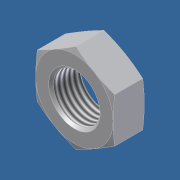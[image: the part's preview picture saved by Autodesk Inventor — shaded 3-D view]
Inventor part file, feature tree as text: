
AUTODESK INVENTOR PART (.ipt)
format: ipt  version: 2012 (Build 160160000, 160)  size: 129,024 bytes
history: native  units: in
note: dims shown in document units (in); Inventor stores cm internally (conversion verified against a paired STEP export)
features: other x70, sketch x3, revolve x2, extrude x1, thread x1
ambient origin geometry x8: Origin, YZ Plane, XZ Plane, XY Plane, X Axis, Y Axis, Z Axis, Center Point
bodies: Solid1 (feature_tree)
feature tree (77):
  sketch  "Sketch_8"  dims[d0=360.0deg d1=0.38in d2=0.0in]
  sketch  "Sketch_10"  dims[d3=360.0deg d4=0.38in d5=0.0in]
  revolve  "Revolution1"  [1 undecoded]
  extrude  "Extrusion1"  Depth=0.38in TaperAngle=0.0deg
  revolve  "Revolution2"  [1 undecoded]
  thread  "Thread1"  [1 undecoded]
  other  "NUT_XY"
  other  "NUT_YZ"
  other  "NUT_ZX"
  other  "NUT_X"
  other  "NUT_Y"
  other  "NUT_Z"
  other  "NUT_Center"
  other  "a1_XY"
  other  "a1_YZ"
  other  "a1_ZX"
  other  "a1_X"
  other  "a1_Y"
  other  "a1_Z"
  other  "a1_Center"
  other  "a2_XY"
  other  "a2_YZ"
  other  "a2_ZX"
  other  "a2_X"
  other  "a2_Y"
  other  "a2_Z"
  other  "a2_Center"
  other  "b1_XY"
  other  "b1_YZ"
  other  "b1_ZX"
  other  "b1_X"
  other  "b1_Y"
  other  "b1_Z"
  other  "b1_Center"
  other  "b2_XY"
  other  "b2_YZ"
  other  "b2_ZX"
  other  "b2_X"
  other  "b2_Y"
  other  "b2_Z"
  other  "b2_Center"
  other  "e_XY"
  other  "e_YZ"
  other  "e_ZX"
  other  "e_X"
  other  "e_Y"
  other  "e_Z"
  other  "e_Center"
  other  "th1_XY"
  other  "th1_YZ"
  other  "th1_ZX"
  other  "th1_X"
  other  "th1_Y"
  other  "th1_Z"
  other  "th1_Center"
  other  "th2_XY"
  other  "th2_YZ"
  other  "th2_ZX"
  other  "th2_X"
  other  "th2_Y"
  other  "th2_Z"
  other  "th2_Center"
  other  "ol1_XY"
  other  "ol1_YZ"
  other  "ol1_ZX"
  other  "ol1_X"
  other  "ol1_Y"
  other  "ol1_Z"
  other  "ol1_Center"
  other  "ol2_XY"
  other  "ol2_YZ"
  other  "ol2_ZX"
  other  "ol2_X"
  other  "ol2_Y"
  other  "ol2_Z"
  other  "ol2_Center"
  sketch  "Sketch_11"
note: 3 required parameter values undecoded (feature->parameter linkage not recoverable at this tier; creation-order binding heuristic only, values carry confidence <= 0.55)